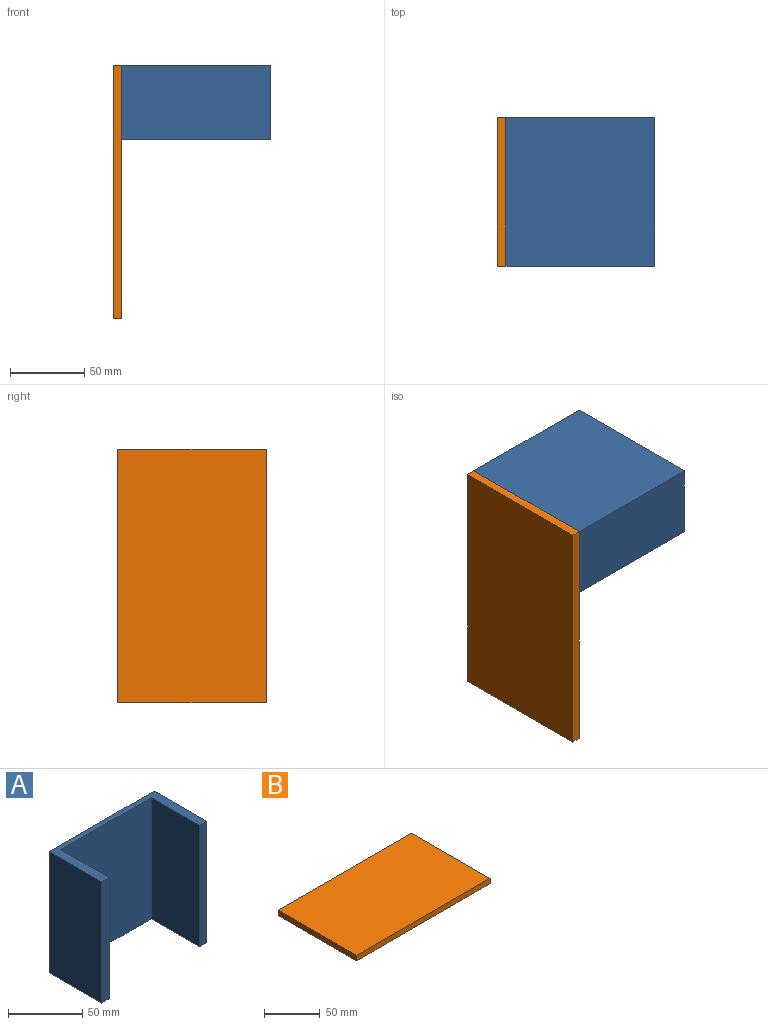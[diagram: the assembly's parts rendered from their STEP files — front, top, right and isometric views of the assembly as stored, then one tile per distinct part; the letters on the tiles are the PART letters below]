
ASSEMBLY  parts=2 mates=1
PART A: 10 faces, bbox 100x50x100 mm
  f0: plane 100x46mm, normal (-1,0,0), area 4600mm2, adj f1,f7,f8,f9
  f1: plane 100x7mm, normal (0,-1,0), area 700mm2, adj f0,f2,f8,f9
  f2: plane 100x50mm, normal (1,0,0), area 5000mm2, adj f1,f3,f8,f9
  f3: plane 100x100mm, normal (0,1,0), area 10000mm2, adj f2,f4,f8,f9
  f4: plane 100x50mm, normal (-1,0,0), area 5000mm2, adj f3,f5,f8,f9
  f5: plane 100x7mm, normal (0,-1,0), area 700mm2, adj f4,f6,f8,f9
  f6: plane 100x46mm, normal (1,0,0), area 4600mm2, adj f5,f7,f8,f9
  f7: plane 100x86mm, normal (0,-1,0), area 8600mm2, adj f0,f6,f8,f9
  f8: plane 100x50mm, normal (0,0,1), area 1044mm2, adj f0,f1,f2,f3,f4,f5,f6,f7
  f9: plane 100x50mm, normal (0,0,-1), area 1044mm2, adj f0,f1,f2,f3,f4,f5,f6,f7
PART B: 6 faces, bbox 170x100x6 mm
  f0: plane 170x6mm, normal (0,1,0), area 1020mm2, adj f1,f3,f4,f5
  f1: plane 100x6mm, normal (-1,0,0), area 600mm2, adj f0,f2,f4,f5
  f2: plane 170x6mm, normal (0,-1,0), area 1020mm2, adj f1,f3,f4,f5
  f3: plane 100x6mm, normal (1,0,0), area 600mm2, adj f0,f2,f4,f5
  f4: plane 170x100mm, normal (0,0,1), area 17000mm2, adj f0,f1,f2,f3
  f5: plane 170x100mm, normal (0,0,-1), area 17000mm2, adj f0,f1,f2,f3
PLACE A rot(axis=(0.58,0.58,0.58),120deg) t=(-289.39,-10.29,53.46)mm
PLACE B rot(axis=(-0.71,0,-0.71),180deg) t=(-295.39,-35.88,-11.09)mm
MATE planar B.f4 <-> A.f9  axis (1,0,0) through (-289.39,-10.29,78.46)mm
